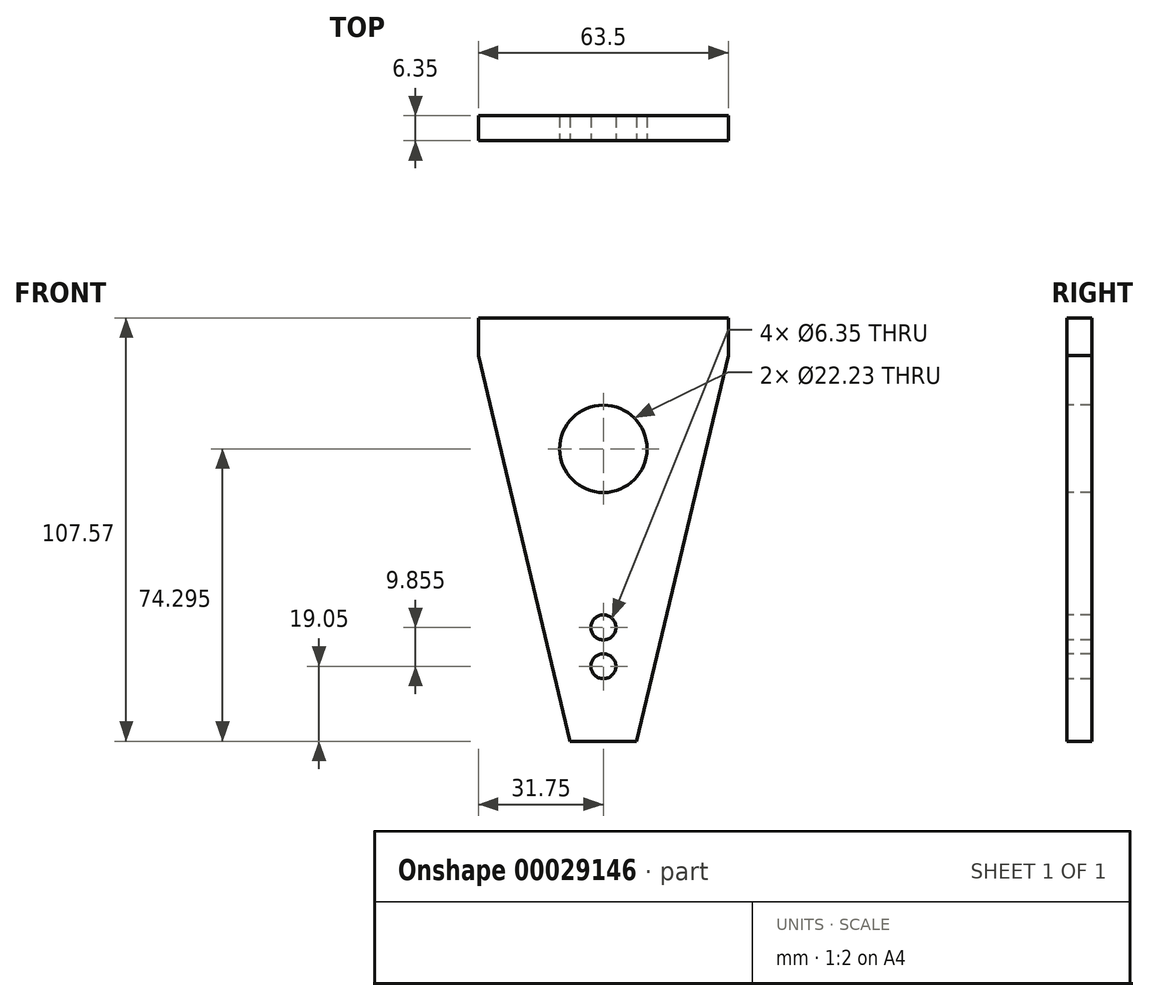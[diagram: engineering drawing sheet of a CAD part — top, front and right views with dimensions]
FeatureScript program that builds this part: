
annotation { "Feature Type Name" : "Feature", "Feature Type Description" : "" }
export const myFeature = defineFeature(function(context is Context, id is Id, definition is map)
    precondition{}
    {
        {
            var Q0;
            Q0=qCreatedBy(makeId("Front.planeOp"),FACE);
            var sketch = newSketch(context, id + "F0", { "sketchPlane" : qUnion([Q0])});
            skLineSegment(sketch, "E0.bottom", {"start": v(0, 0) * mm, "end": v(63.5, 0) * mm});
            skLineSegment(sketch, "E0.top", {"start": v(0, 107.57) * mm, "end": v(63.5, 107.57) * mm});
            skLineSegment(sketch, "E0.left", {"start": v(0, 0) * mm, "end": v(0, 107.57) * mm});
            skLineSegment(sketch, "E0.right", {"start": v(63.5, 0) * mm, "end": v(63.5, 107.57) * mm});
            skPoint(sketch, "E1", {"position": v(63.5, 98.04) * mm});
            skPoint(sketch, "E2", {"position": v(54.66, 107.57) * mm});
            skSolve(sketch);
        }
        {
            var Q0;
            Q0=makeQuery(id+"F0.imprint","IMPRINT",FACE,{"disambiguationData":[TD([[makeQuery(id+"F0.imprint","IMPRINT",EDGE,{"derivedFrom":sQuery(id+"F0.wireOp",EDGE,"E0.bottom")}),1.0]])]});
            extrude(context, id + "F1", {"entities" : qUnion([Q0]), "depth" : 6.35 * mm});
        }
        {
            var Q0;
            Q0=makeQuery(id+"F1.opExtrude","CAP_FACE",FACE,{"disambiguationData":[OSD([sQuery(id+"F0.wireOp",EDGE,"E0.bottom"),sQuery(id+"F0.wireOp",EDGE,"E0.top"),sQuery(id+"F0.wireOp",EDGE,"E0.left"),sQuery(id+"F0.wireOp",EDGE,"E0.right")])],"isStart":false});
            var sketch = newSketch(context, id + "F2", { "sketchPlane" : qUnion([Q0])});
            skPoint(sketch, "E3", {"position": v(63.5, 98.04) * mm});
            skPoint(sketch, "E4", {"position": v(0, 98.04) * mm});
            skPoint(sketch, "E5", {"position": v(31.75, 0) * mm});
            skPoint(sketch, "E6", {"position": v(23.3, 0) * mm});
            skPoint(sketch, "E7", {"position": v(40.2, 0) * mm});
            skLineSegment(sketch, "E8", {"start": v(0, 98.04) * mm, "end": v(23.3, 0) * mm});
            skLineSegment(sketch, "E9", {"start": v(40.2, 0) * mm, "end": v(63.5, 98.04) * mm});
            skSolve(sketch);
        }
        {
            var Q0;
            {var subQ1=sQuery(id+"F2.wireOp",EDGE,"E8");Q0=makeQuery(id+"F2.imprint","IMPRINT",FACE,{"disambiguationData":[TD([[makeQuery(id+"F2.imprint","IMPRINT",EDGE,{"derivedFrom":subQ1}),-1.0]])]});}
            var Q1;
            {var subQ1=sQuery(id+"F2.wireOp",EDGE,"E9");Q1=makeQuery(id+"F2.imprint","IMPRINT",FACE,{"disambiguationData":[TD([[makeQuery(id+"F2.imprint","IMPRINT",EDGE,{"derivedFrom":subQ1}),-1.0]])]});}
            extrude(context, id + "F3", {"entities" : qUnion([Q0, Q1]), "operationType" : NewBodyOperationType.REMOVE, "endBound" : BoundingType.THROUGH_ALL, "oppositeDirection" : true, "depth" : 25.4 * mm});
        }
        {
            var Q0;
            Q0=makeQuery(id+"F1.opExtrude","CAP_FACE",FACE,{"disambiguationData":[OSD([sQuery(id+"F0.wireOp",EDGE,"E0.bottom"),sQuery(id+"F0.wireOp",EDGE,"E0.top"),sQuery(id+"F0.wireOp",EDGE,"E0.left"),sQuery(id+"F0.wireOp",EDGE,"E0.right")])],"isStart":false});
            var sketch = newSketch(context, id + "F4", { "sketchPlane" : qUnion([Q0])});
            skPoint(sketch, "E10", {"position": v(31.75, 107.57) * mm});
            skCircle(sketch, "E11", {"center": v(31.75, 74.3) * mm, "radius": 11.11 * mm});
            skCircle(sketch, "E12", {"center": v(31.75, 28.9) * mm, "radius": 3.18 * mm});
            skCircle(sketch, "E13", {"center": v(31.75, 19.05) * mm, "radius": 3.18 * mm});
            skSolve(sketch);
        }
        {
            var Q0;
            Q0=makeQuery(id+"F4.imprint","IMPRINT",FACE,{"disambiguationData":[TD([[makeQuery(id+"F4.imprint","IMPRINT",EDGE,{"derivedFrom":sQuery(id+"F4.wireOp",EDGE,"E11")}),1.0]])]});
            var Q1;
            Q1=makeQuery(id+"F4.imprint","IMPRINT",FACE,{"disambiguationData":[TD([[makeQuery(id+"F4.imprint","IMPRINT",EDGE,{"derivedFrom":sQuery(id+"F4.wireOp",EDGE,"E12")}),1.0]])]});
            var Q2;
            Q2=makeQuery(id+"F4.imprint","IMPRINT",FACE,{"disambiguationData":[TD([[makeQuery(id+"F4.imprint","IMPRINT",EDGE,{"derivedFrom":sQuery(id+"F4.wireOp",EDGE,"E13")}),1.0]])]});
            extrude(context, id + "F5", {"entities" : qUnion([Q0, Q1, Q2]), "operationType" : NewBodyOperationType.REMOVE, "oppositeDirection" : true, "depth" : 25.4 * mm});
        }
    });
